SOLIDWORKS PART (.sldprt)
format: sldprt  version: not decoded by parser v0  size: 343,552 bytes
history: native  units: mm
features: sketch x11, extrude x7, chamfer x5, cut_extrude x4, material x1 (+13 scaffold rows collapsed)
feature tree (41):
  scaffold x13  (default folders/planes/origin — collapsed)
  material  "Material <not specified>"
  sketch  "Sketch1"  dims[D1=4.0mm D2=4.0mm D3=4.0mm D4=3.0mm D5=5.0mm D6=8.0mm]
  extrude  "Boss-Extrude1"  Depth=4mm
  extrude  "Boss-Extrude2"  [1 undecoded]
  sketch  "Sketch1<5>"
  sketch  "Sketch2"  dims[D1=3.0mm D2=3.0mm]
  extrude  "Boss-Extrude3"  [1 undecoded]
  sketch  "Sketch3"  dims[D1=9.1mm]
  extrude  "Boss-Extrude4"  [1 undecoded]
  sketch  "Sketch4"  dims[c1.D1=3.0mm c1.D2=4.7625mm c2.D1=3.0mm c2.D2=0.25mm]
  extrude  "Boss-Extrude5"  [1 undecoded]
  sketch  "Sketch5"  dims[D1=15.0mm D2=0.5mm D3=0.5mm D4=0.0327mm]
  extrude  "Boss-Extrude6"  Depth=3mm
  chamfer  "Chamfer1"  Distance=4mm Angle=45deg
  chamfer  "Chamfer4"  Distance=2mm Angle=45deg
  chamfer  "Chamfer5"  Distance=1mm Angle=45deg
  sketch  "Sketch6"  dims[D1=0.5mm D2=0.5mm D3=6.2315mm]
  extrude  "Boss-Extrude7"  Depth=3mm
  chamfer  "Chamfer8"  Distance=3mm Angle=45deg
  chamfer  "Chamfer7"  Distance=1mm Angle=45deg
  sketch  "Sketch7"  dims[D1=2.2mm]
  cut_extrude  "Cut-Extrude1"  [1 undecoded]
  sketch  "Sketch8"  dims[D1=2.2mm]
  cut_extrude  "Cut-Extrude2"  [1 undecoded]
  sketch  "Sketch9"  dims[D1=2.2mm]
  cut_extrude  "Cut-Extrude3"  [1 undecoded]
  sketch  "Sketch10"  dims[D1=2.2mm]
  cut_extrude  "Cut-Extrude4"  [1 undecoded]
decode coverage: 18 of 27 modeling features carry decoded parameters
note: 8 parameter values undecoded
summary: no parameter record found for 8 features
note: suppression state not decoded; provenance and decode notes live in map.json
